# Revit family: EU_ID-Single
name_source: partatom
category: Doors
revit_build: Autodesk Revit 2014 (Build: 20130308_1515(x64)
units: mm (PartAtom-declared; Revit-internal decimal feet)

## types (6) — shared parameters
Doorleaf = Dorblad hvit
Doornobb = EU_General-Metal
Frame = EU_General-Frame
Frame Depth = 100 mm  [stored 0.328084 ft]
Frame Thickness = 40 mm  [stored 0.131234 ft]
Function = Interior
Rough Height = 21 mm
Treshold = EU_General-Wood
Wall Closure = By host

## per-type parameters (varying)
| type | Height | Rough Width | Type Name (in Project) | Width |
| 7x21 | 2110 mm  [stored 6.92257 ft] | 7 mm  [stored 0.0229659 ft] |  | 710 mm |
| 8x21 | 2110 mm  [stored 6.92257 ft] | 8 mm  [stored 0.0262467 ft] |  | 810 mm |
| 9x21 | 2110 mm  [stored 6.92257 ft] | 9 mm | Type name | 910 mm |
| 10x21 | 2110 mm  [stored 6.92257 ft] | 10 mm  [stored 0.0328084 ft] | Type name | 1010 mm  [stored 3.31365 ft] |
| 11x21 | 2115 mm  [stored 6.93898 ft] | 11 mm | Type name | 1110 mm  [stored 3.64173 ft] |
| 12x21 | 2115 mm  [stored 6.93898 ft] | 12 mm  [stored 0.0393701 ft] |  | 1210 mm  [stored 3.96982 ft] |

note: [stored X ft] marks values corroborated as IEEE doubles in the binary element streams (Revit-internal decimal feet)
